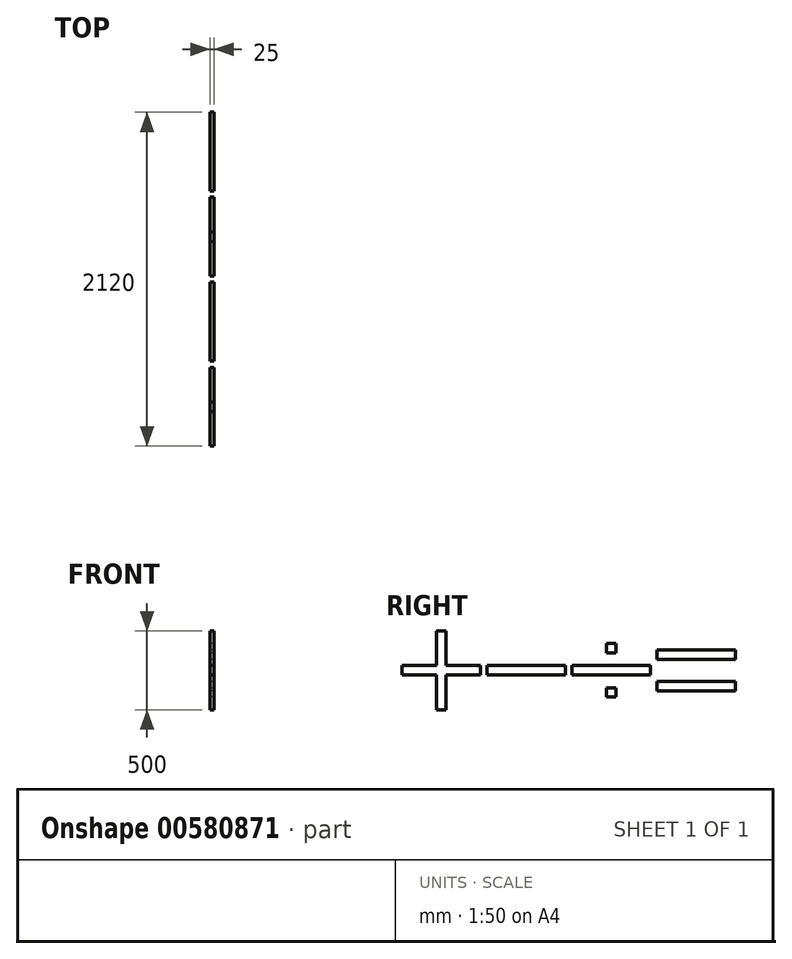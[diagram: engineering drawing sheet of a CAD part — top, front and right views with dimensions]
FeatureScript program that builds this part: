
annotation { "Feature Type Name" : "Feature", "Feature Type Description" : "" }
export const myFeature = defineFeature(function(context is Context, id is Id, definition is map)
    precondition{}
    {
        {
            var Q0;
            Q0=qCreatedBy(makeId("Right.planeOp"),FACE);
            var sketch = newSketch(context, id + "F0", { "sketchPlane" : qUnion([Q0])});
            skLineSegment(sketch, "E0.bottom", {"start": v(-792.74, 212.7) * mm, "end": v(-732.74, 212.7) * mm});
            skLineSegment(sketch, "E0.left", {"start": v(-1012.74, -7.3) * mm, "end": v(-1012.74, -37.3) * mm});
            skLineSegment(sketch, "E1.left", {"start": v(-1012.74, -7.3) * mm, "end": v(-1012.74, -67.3) * mm});
            skLineSegment(sketch, "E1.right", {"start": v(-512.74, -7.3) * mm, "end": v(-512.74, -67.3) * mm});
            skLineSegment(sketch, "E2.right", {"start": v(67.26, -7.3) * mm, "end": v(67.26, -67.3) * mm});
            skLineSegment(sketch, "E3.right", {"start": v(567.26, -7.3) * mm, "end": v(567.26, -67.3) * mm});
            skLineSegment(sketch, "E4.bottom", {"start": v(-792.74, -287.3) * mm, "end": v(-762.74, -287.3) * mm});
            skLineSegment(sketch, "E4.right", {"start": v(-512.74, -67.3) * mm, "end": v(-512.74, -37.3) * mm});
            skLineSegment(sketch, "E5.bottom", {"start": v(-1012.74, -7.3) * mm, "end": v(-792.74, -7.3) * mm});
            skLineSegment(sketch, "E5.top", {"start": v(-1012.74, -67.3) * mm, "end": v(-792.74, -67.3) * mm});
            skLineSegment(sketch, "E6.bottom", {"start": v(-792.74, 212.7) * mm, "end": v(-762.74, 212.7) * mm});
            skLineSegment(sketch, "E7.top", {"start": v(-792.74, -287.3) * mm, "end": v(-732.74, -287.3) * mm});
            skLineSegment(sketch, "E7.left", {"start": v(-792.74, 212.7) * mm, "end": v(-792.74, -7.3) * mm});
            skLineSegment(sketch, "E7.right", {"start": v(-732.74, 212.7) * mm, "end": v(-732.74, -7.3) * mm});
            skLineSegment(sketch, "E8.left", {"start": v(-512.74, -67.3) * mm, "end": v(-512.74, -7.3) * mm});
            skLineSegment(sketch, "E8.right", {"start": v(-472.74, -67.3) * mm, "end": v(-472.74, -7.3) * mm});
            skLineSegment(sketch, "E9.right", {"start": v(27.26, -7.3) * mm, "end": v(27.26, -67.3) * mm});
            skLineSegment(sketch, "E10", {"start": v(-472.74, -7.3) * mm, "end": v(27.26, -7.3) * mm});
            skLineSegment(sketch, "E11", {"start": v(-472.74, -67.3) * mm, "end": v(27.26, -67.3) * mm});
            skLineSegment(sketch, "E12.trimOffspring", {"start": v(-732.74, -7.3) * mm, "end": v(-512.74, -7.3) * mm});
            skLineSegment(sketch, "E13.trimOffspring", {"start": v(-732.74, -67.3) * mm, "end": v(-512.74, -67.3) * mm});
            skLineSegment(sketch, "E14.trimOffspring", {"start": v(-792.74, -67.3) * mm, "end": v(-792.74, -287.3) * mm});
            skLineSegment(sketch, "E15.trimOffspring", {"start": v(-732.74, -67.3) * mm, "end": v(-732.74, -287.3) * mm});
            skLineSegment(sketch, "E16", {"start": v(67.26, -7.3) * mm, "end": v(567.26, -7.3) * mm});
            skLineSegment(sketch, "E17", {"start": v(67.26, -67.3) * mm, "end": v(567.26, -67.3) * mm});
            skLineSegment(sketch, "E18.bottom", {"start": v(67.26, -7.3) * mm, "end": v(317.26, -7.3) * mm});
            skLineSegment(sketch, "E18.top", {"start": v(67.26, -67.3) * mm, "end": v(317.26, -67.3) * mm});
            skLineSegment(sketch, "E19", {"start": v(317.26, 72.7) * mm, "end": v(317.26, 132.7) * mm});
            skLineSegment(sketch, "E20", {"start": v(317.26, 72.7) * mm, "end": v(317.26, 102.7) * mm});
            skLineSegment(sketch, "E21.bottom", {"start": v(287.26, -147.3) * mm, "end": v(347.26, -147.3) * mm});
            skLineSegment(sketch, "E21.top", {"start": v(287.26, -207.3) * mm, "end": v(347.26, -207.3) * mm});
            skLineSegment(sketch, "E21.left", {"start": v(287.26, -147.3) * mm, "end": v(287.26, -207.3) * mm});
            skLineSegment(sketch, "E21.right", {"start": v(347.26, -147.3) * mm, "end": v(347.26, -207.3) * mm});
            skLineSegment(sketch, "E22.bottom", {"start": v(287.26, 132.7) * mm, "end": v(347.26, 132.7) * mm});
            skLineSegment(sketch, "E22.top", {"start": v(287.26, 72.7) * mm, "end": v(347.26, 72.7) * mm});
            skLineSegment(sketch, "E22.left", {"start": v(287.26, 132.7) * mm, "end": v(287.26, 72.7) * mm});
            skLineSegment(sketch, "E22.right", {"start": v(347.26, 132.7) * mm, "end": v(347.26, 72.7) * mm});
            skLineSegment(sketch, "E23.right", {"start": v(607.26, 92.7) * mm, "end": v(607.26, 32.7) * mm});
            skLineSegment(sketch, "E24.right", {"start": v(1107.26, 92.7) * mm, "end": v(1107.26, 32.7) * mm});
            skLineSegment(sketch, "E25.bottom", {"start": v(607.26, -107.3) * mm, "end": v(1107.26, -107.3) * mm});
            skLineSegment(sketch, "E25.top", {"start": v(607.26, -167.3) * mm, "end": v(1107.26, -167.3) * mm});
            skLineSegment(sketch, "E25.left", {"start": v(607.26, -107.3) * mm, "end": v(607.26, -167.3) * mm});
            skLineSegment(sketch, "E25.right", {"start": v(1107.26, -107.3) * mm, "end": v(1107.26, -167.3) * mm});
            skLineSegment(sketch, "E26.bottom", {"start": v(607.26, 92.7) * mm, "end": v(1107.26, 92.7) * mm});
            skLineSegment(sketch, "E26.top", {"start": v(607.26, 32.7) * mm, "end": v(1107.26, 32.7) * mm});
            skPoint(sketch, "E27.orphan", {"position": v(1147.26, -287.3) * mm});
            skPoint(sketch, "E28.orphan", {"position": v(567.26, -287.3) * mm});
            skPoint(sketch, "E29.orphan", {"position": v(317.26, -177.3) * mm});
            skPoint(sketch, "E30.orphan", {"position": v(317.26, -287.3) * mm});
            skPoint(sketch, "E31.orphan", {"position": v(317.26, 212.7) * mm});
            skPoint(sketch, "E32.trimOffspring.end.orphan", {"position": v(567.26, 212.7) * mm});
            skPoint(sketch, "E33.orphan", {"position": v(67.26, -287.3) * mm});
            skPoint(sketch, "E34.orphan", {"position": v(67.26, 212.7) * mm});
            skPoint(sketch, "E35.orphan", {"position": v(-512.74, -287.3) * mm});
            skPoint(sketch, "E36.orphan", {"position": v(-512.74, 212.7) * mm});
            skLineSegment(sketch, "E37.trimOffspring", {"start": v(-1012.74, -67.3) * mm, "end": v(-1012.74, -37.3) * mm});
            skPoint(sketch, "E38.orphan", {"position": v(-1012.74, -287.3) * mm});
            skSolve(sketch);
        }
        {
            var Q0;
            Q0 = qSketchRegion(id + "F0", true);
            extrude(context, id + "F1", {"entities" : qUnion([Q0]), "depth" : 25 * mm, "offsetDistance" : 25 * mm});
        }
    });
